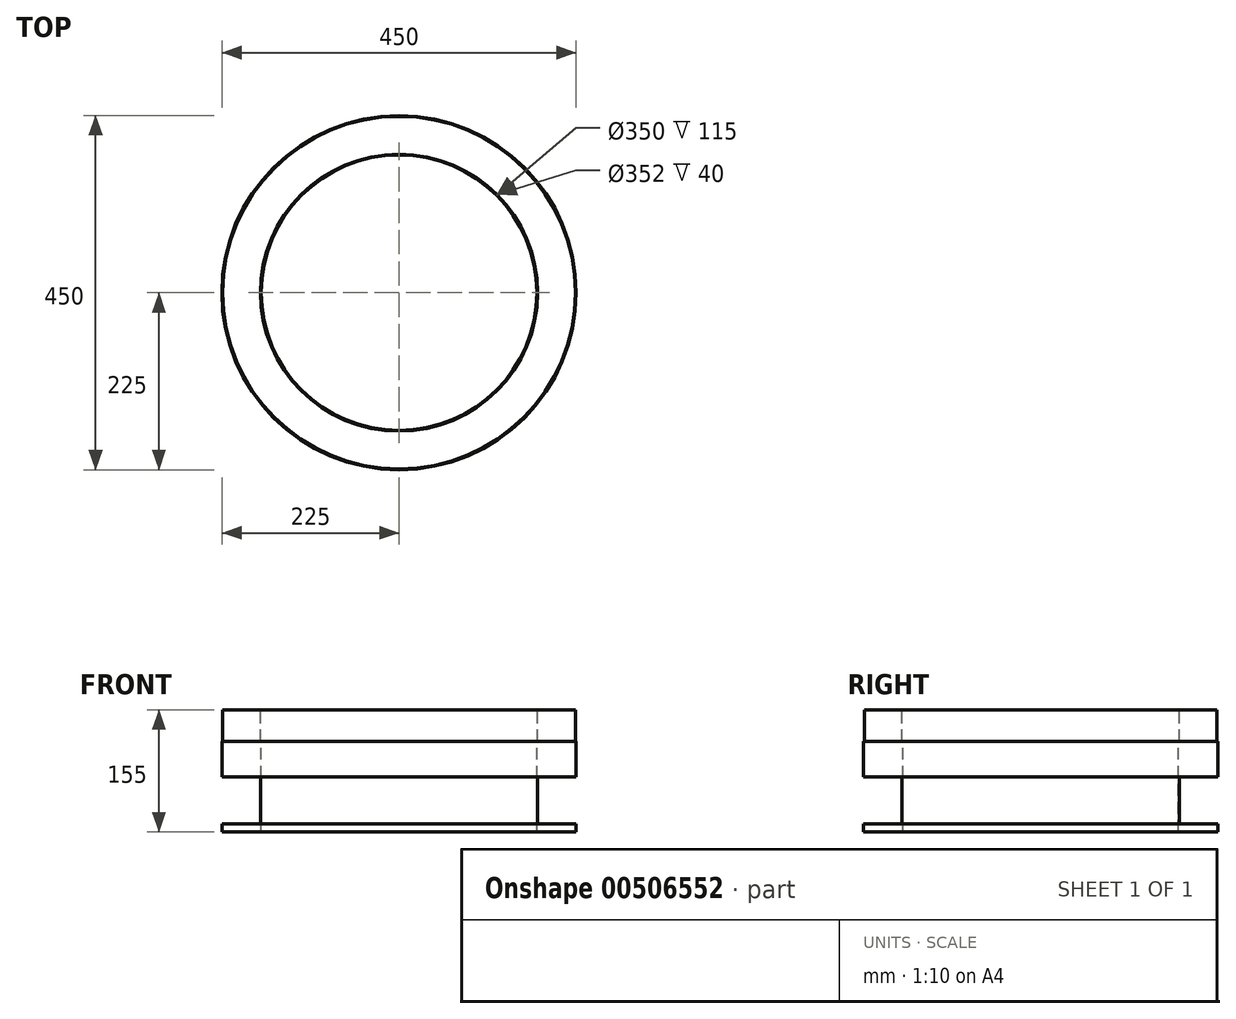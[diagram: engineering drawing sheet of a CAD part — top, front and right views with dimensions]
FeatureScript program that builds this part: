
annotation { "Feature Type Name" : "Feature", "Feature Type Description" : "" }
export const myFeature = defineFeature(function(context is Context, id is Id, definition is map)
    precondition{}
    {
        {
            var Q0;
            Q0=qCreatedBy(makeId("Front.planeOp"),FACE);
            var sketch = newSketch(context, id + "F0", { "sketchPlane" : qUnion([Q0])});
            skLineSegment(sketch, "E0", {"start": v(0, 710.75) * mm, "end": v(0, -704.58) * mm, "construction": true});
            skLineSegment(sketch, "E1", {"start": v(-175, 300.65) * mm, "end": v(-175, 415.65) * mm});
            skLineSegment(sketch, "E2", {"start": v(-175, 415.65) * mm, "end": v(-176, 415.65) * mm});
            skLineSegment(sketch, "E3", {"start": v(-224, 415.65) * mm, "end": v(-225, 415.65) * mm});
            skLineSegment(sketch, "E4", {"start": v(-225, 415.65) * mm, "end": v(-225, 370.65) * mm});
            skLineSegment(sketch, "E5", {"start": v(-225, 370.65) * mm, "end": v(-176, 370.65) * mm});
            skLineSegment(sketch, "E6", {"start": v(-176, 370.65) * mm, "end": v(-176, 310.65) * mm});
            skLineSegment(sketch, "E7", {"start": v(-176, 310.65) * mm, "end": v(-225, 310.65) * mm});
            skLineSegment(sketch, "E8", {"start": v(-225, 310.65) * mm, "end": v(-225, 300.65) * mm});
            skLineSegment(sketch, "E9", {"start": v(-225, 300.65) * mm, "end": v(-175, 300.65) * mm});
            skLineSegment(sketch, "E10", {"start": v(-224, 455.65) * mm, "end": v(-224, 415.65) * mm});
            skLineSegment(sketch, "E11", {"start": v(-224, 455.65) * mm, "end": v(-176, 455.65) * mm});
            skLineSegment(sketch, "E12", {"start": v(-176, 415.65) * mm, "end": v(-176, 455.65) * mm});
            skSolve(sketch);
        }
        {
            var Q0;
            Q0=qSketchRegion(id+"F0",true);
            var Q1;
            Q1=sQuery(id+"F0.wireOp",EDGE,"E0");
            revolve(context, id + "F1", {"entities" : qUnion([Q0]), "axis" : qUnion([Q1]), "revolveType" : RevolveType.FULL});
        }
    });
